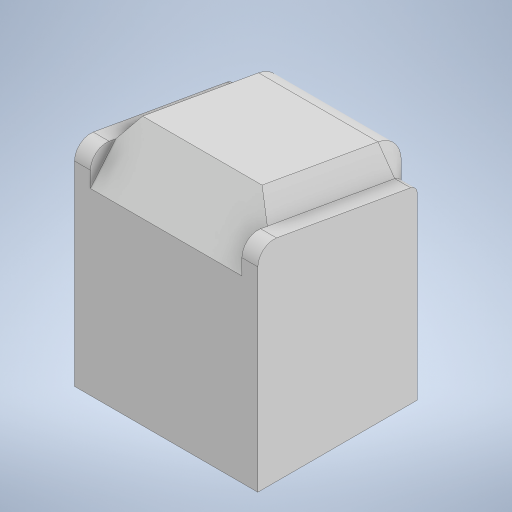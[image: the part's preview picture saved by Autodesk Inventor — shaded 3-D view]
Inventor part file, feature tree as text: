
AUTODESK INVENTOR PART (.ipt)
format: ipt  version: 2024 (Build 280153000, 153)  size: 337,408 bytes
history: native  units: mm
features: sketch x8, extrude x6, projected_geometry x6, fillet x5, plane x3, revolve x1, mirror x1
ambient origin geometry x8: Origin, YZ Plane, XZ Plane, XY Plane, X Axis, Y Axis, Z Axis, Center Point
bodies: Solid1 (feature_tree)
feature tree (30):
  extrude  "Extrusion1"  Depth=400.0mm
  revolve  "Revolution1"  [1 undecoded]
  sketch  "Sketch3"  dims[d4=120.0deg d5=135.0deg d7=450.0mm d8=0.0mm]
  plane  "Work Plane4"
  extrude  "Extrusion7"  TaperAngle=135.0deg  [1 undecoded]
  fillet  "Fillet6"  Radius=450.0mm
  mirror  "Mirror1"
  plane  "Work Plane5"
  extrude  "Extrusion8"  Depth=20.0mm
  extrude  "Extrusion9"  Depth=10.0mm TaperAngle=0.0deg
  sketch  "Sketch8"  dims[d23=10.0mm d24=0.0mm d25=20.0mm]
  extrude  "Extrusion5"  Depth=20.0mm
  extrude  "Extrusion6"  Depth=50.857864mm
  fillet  "Fillet1"  Radius=2.0mm
  fillet  "Fillet3"  [1 undecoded]
  fillet  "Fillet4"  Radius=10.0mm
  fillet  "Fillet5"  Radius=50.857864mm
  sketch  "Sketch1"  dims[d0=460.0mm d1=400.0mm]
  sketch  "Sketch2"  dims[d2=40.0mm d3=40.0mm]
  projected_geometry  "Projected Loop1"
  projected_geometry  "Projected Loop2"
  plane  "Work Plane3"
  sketch  "Sketch6"  dims[d9=20.0mm d10=13.962634mm]
  projected_geometry  "Projected Loop4"
  sketch  "Sketch7"  dims[d17=150.0deg d20=-10.0mm d21=10.0mm d22=0.0mm]
  projected_geometry  "Projected Loop5"
  sketch  "Sketch9"  dims[d27=2.0mm d28=2.0mm d29=2.0mm d30=67.5deg d32=10.0mm d34=50.857864mm]
  projected_geometry  "Projected Loop6"
  sketch  "Sketch11"  dims[d35=40.0mm d36=40.0mm d37=300.0mm d38=250.0mm d39=60.0mm d40=40.0mm d41=40.0mm d42=40.0mm d43=40.0mm d44=40.0mm d45=40.0mm d46=80.0mm d47=40.0mm d48=10.0mm d50=10.0mm d51=3.0mm d52=39.0mm d53=40.0mm d54=20.0mm d55=55.0mm d56=105.0mm d57=90.0mm d58=220.0mm d59=8.0mm d60=20.0mm d61=55.0mm d62=210.0mm d63=200.0mm d64=160.0mm d65=118.0mm d66=1.0mm d67=40.0mm d68=0.0mm d69=40.0mm d70=150.0deg d71=40.0mm d72=0.0mm d73=10.0mm d74=0.0mm]
  projected_geometry  "Projected Loop7"
note: 3 required parameter values undecoded (feature->parameter linkage not recoverable at this tier; creation-order binding heuristic only, values carry confidence <= 0.55)